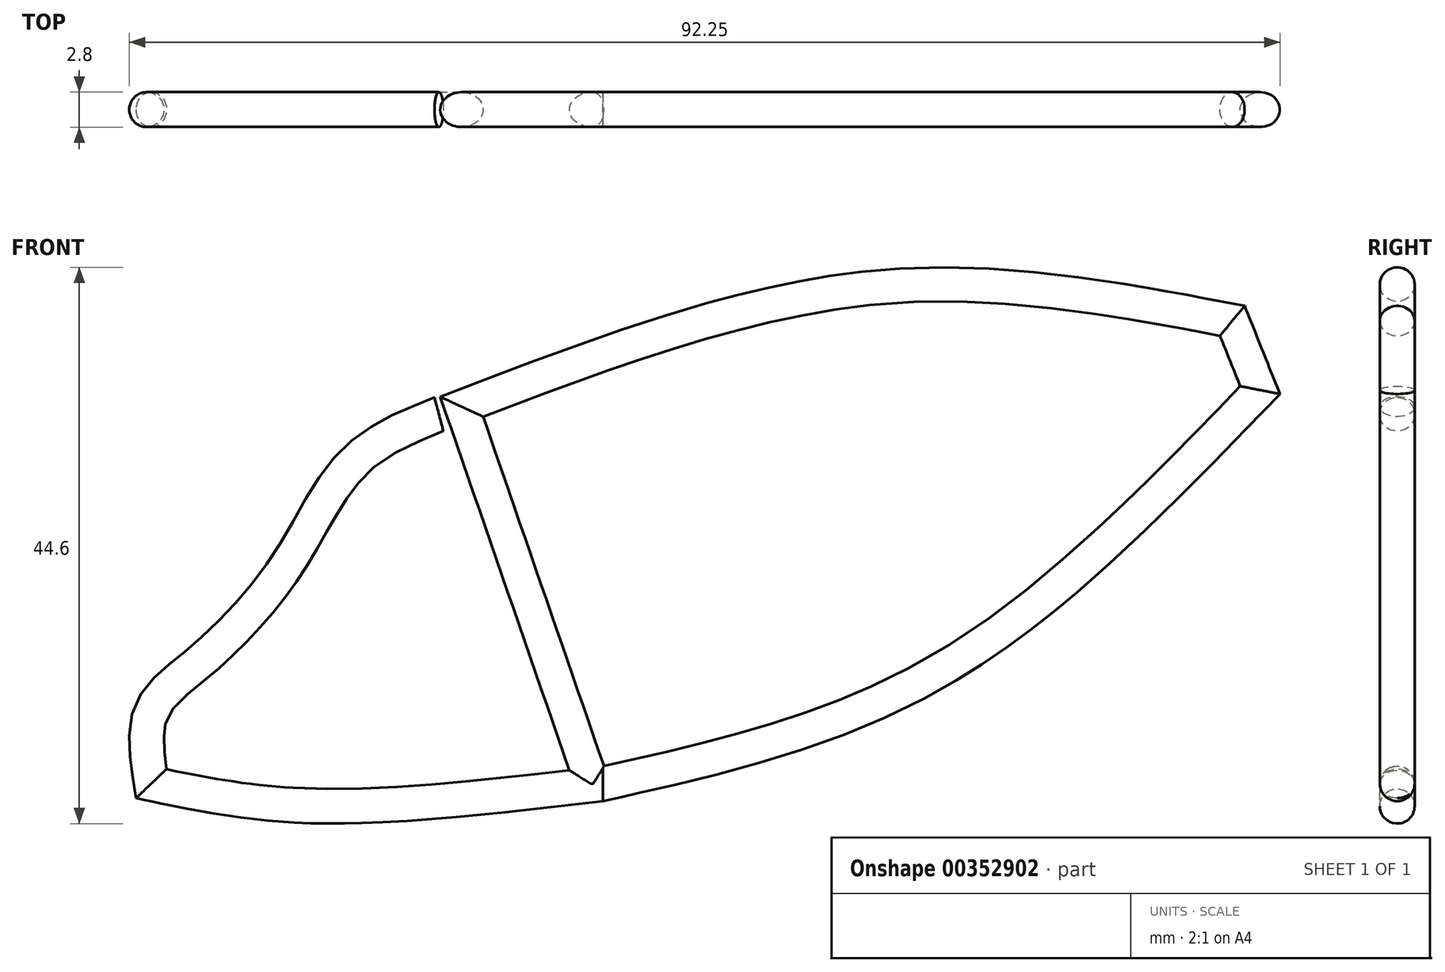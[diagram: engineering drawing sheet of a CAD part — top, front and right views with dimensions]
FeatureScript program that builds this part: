
annotation { "Feature Type Name" : "Feature", "Feature Type Description" : "" }
export const myFeature = defineFeature(function(context is Context, id is Id, definition is map)
    precondition{}
    {
        {
            var Q0;
            Q0=qCreatedBy(makeId("Right.planeOp"),FACE);
            var sketch = newSketch(context, id + "F0", { "sketchPlane" : qUnion([Q0])});
            skCircle(sketch, "E0", {"center": v(0, 0) * mm, "radius": 1.4 * mm});
            skSolve(sketch);
        }
        {
            var Q0;
            Q0=qCreatedBy(makeId("Front.planeOp"),FACE);
            var sketch = newSketch(context, id + "F1", { "sketchPlane" : qUnion([Q0])});
            skFitSpline(sketch, "E1", {"points": [v(0, 0) * mm, v(26.67, 8.9) * mm, v(52.67, 31.56) * mm], "startDerivative": vector(57.81, 12.95) * mm, "endDerivative": vector(47.7, 49.54) * mm});
            skLineSegment(sketch, "E2", {"start": v(52.67, 31.56) * mm, "end": v(50.45, 37.12) * mm});
            skFitSpline(sketch, "E3", {"points": [v(50.45, 37.12) * mm, v(21.78, 39.78) * mm, v(-11.33, 30.23) * mm], "startDerivative": vector(-59.24, 11.29) * mm, "endDerivative": vector(-64.26, -24.53) * mm});
            skLineSegment(sketch, "E4", {"start": v(-11.33, 30.23) * mm, "end": v(-0.88, 0) * mm});
            skPoint(sketch, "E5.6.internal.orphan", {"position": v(-36.23, 0) * mm});
            skPoint(sketch, "E6.2.internal.orphan", {"position": v(-1.3, 0) * mm});
            skSolve(sketch);
        }
        {
            var Q0;
            Q0=makeQuery(id+"F0.imprint","IMPRINT",FACE,{"disambiguationData":[TD([[makeQuery(id+"F0.imprint","IMPRINT",EDGE,{"derivedFrom":sQuery(id+"F0.wireOp",EDGE,"E0")}),1.0]])]});
            var Q1;
            Q1=sQuery(id+"F1.wireOp",EDGE,"E1");
            var Q2;
            Q2=sQuery(id+"F1.wireOp",EDGE,"E2");
            var Q3;
            Q3=sQuery(id+"F1.wireOp",EDGE,"E3");
            var Q4;
            Q4=sQuery(id+"F1.wireOp",EDGE,"E4");
            sweep(context, id + "F2", {"profiles" : qUnion([Q0]), "path" : qUnion([Q1, Q2, Q3, Q4])});
        }
        {
            var Q0;
            Q0=qCreatedBy(makeId("Right.planeOp"),FACE);
            var sketch = newSketch(context, id + "F3", { "sketchPlane" : qUnion([Q0])});
            skCircle(sketch, "E7", {"center": v(0, 0) * mm, "radius": 1.4 * mm});
            skSolve(sketch);
        }
        {
            var Q0;
            Q0=qCreatedBy(makeId("Front.planeOp"),FACE);
            var sketch = newSketch(context, id + "F4", { "sketchPlane" : qUnion([Q0])});
            skFitSpline(sketch, "E8", {"points": [v(0, 0) * mm, v(-23.56, -1.78) * mm, v(-36.23, 0) * mm], "startDerivative": vector(-44.07, -5.18) * mm, "endDerivative": vector(-27.55, 5.74) * mm});
            skPoint(sketch, "E9.1.internal.orphan", {"position": v(-36.23, 5.78) * mm});
            skPoint(sketch, "E9.2.internal.orphan", {"position": v(-32.33, 9.78) * mm});
            skFitSpline(sketch, "E10", {"points": [v(-36.23, 0) * mm, v(-36.23, 5.78) * mm, v(-32.33, 9.78) * mm, v(-25.34, 17.56) * mm, v(-20, 25.78) * mm, v(-13.16, 29.62) * mm], "startDerivative": vector(-5.55, 36.62) * mm, "endDerivative": vector(37.11, 14.7) * mm});
            skSolve(sketch);
        }
        {
            var Q0;
            Q0=makeQuery(id+"F3.imprint","IMPRINT",FACE,{"disambiguationData":[TD([[makeQuery(id+"F3.imprint","IMPRINT",EDGE,{"derivedFrom":sQuery(id+"F3.wireOp",EDGE,"E7")}),1.0]])]});
            var Q1;
            Q1=sQuery(id+"F4.wireOp",EDGE,"E8");
            var Q2;
            Q2=sQuery(id+"F4.wireOp",EDGE,"E10");
            sweep(context, id + "F5", {"operationType" : NewBodyOperationType.ADD, "profiles" : qUnion([Q0]), "path" : qUnion([Q1, Q2])});
        }
    });
